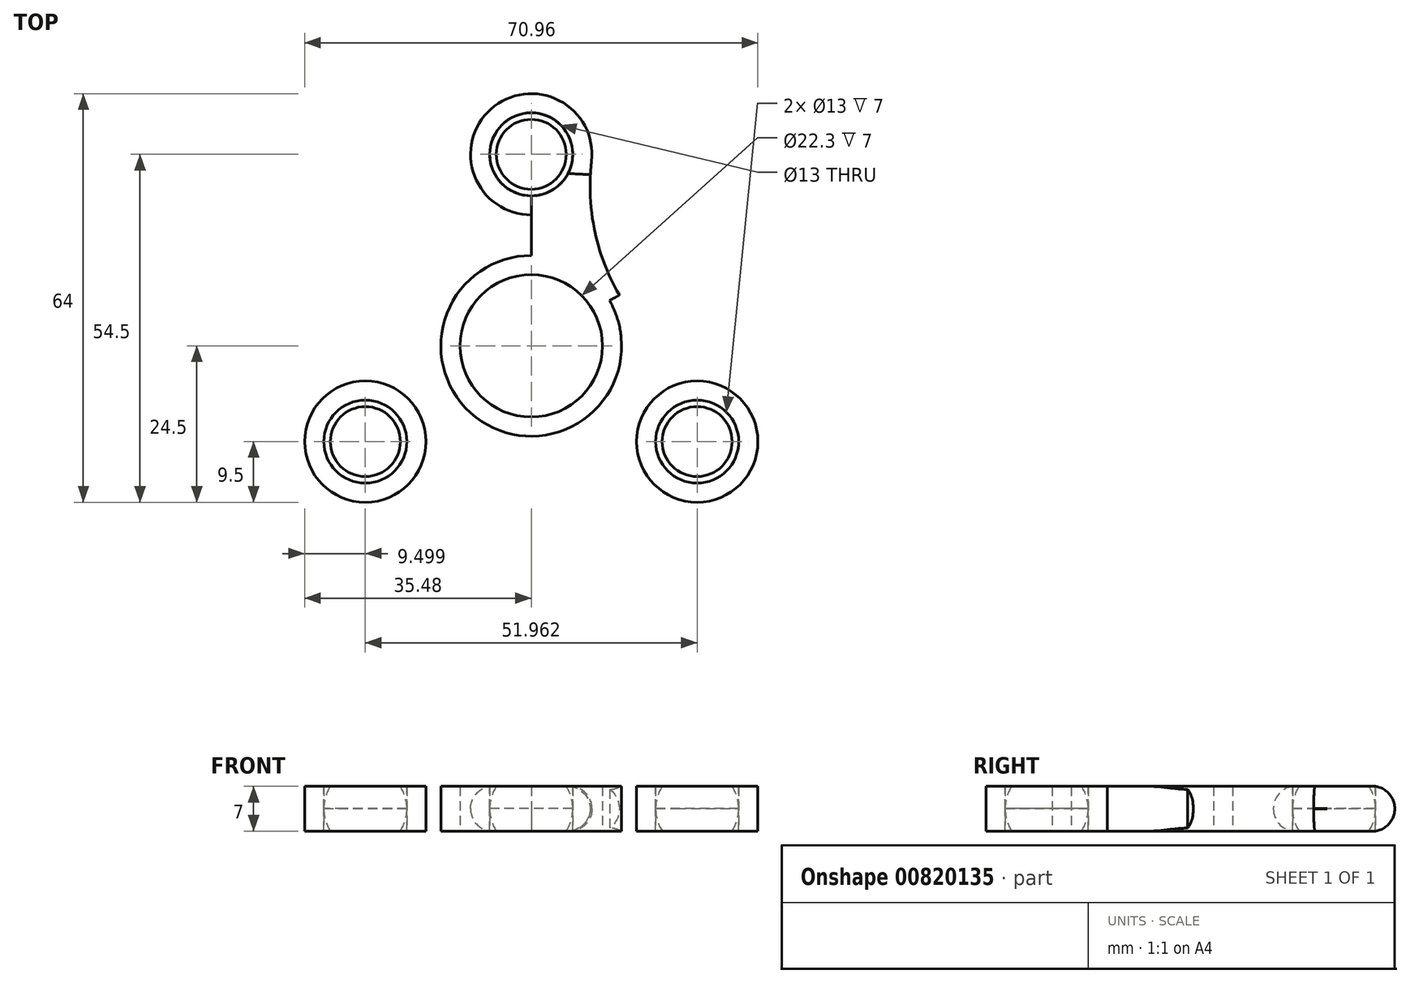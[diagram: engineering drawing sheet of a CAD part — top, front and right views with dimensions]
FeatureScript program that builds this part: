
annotation { "Feature Type Name" : "Feature", "Feature Type Description" : "" }
export const myFeature = defineFeature(function(context is Context, id is Id, definition is map)
    precondition{}
    {
        {
            var Q0;
            Q0=qCreatedBy(makeId("Top.planeOp"),FACE);
            var sketch = newSketch(context, id + "F0", { "sketchPlane" : qUnion([Q0])});
            skCircle(sketch, "E0", {"center": v(0, 0) * mm, "radius": 11.15 * mm});
            skCircle(sketch, "E1", {"center": v(0, 0) * mm, "radius": 14.15 * mm});
            skCircle(sketch, "E2", {"center": v(0, 30) * mm, "radius": 6.5 * mm});
            skCircle(sketch, "E3", {"center": v(0, 30) * mm, "radius": 9.5 * mm});
            skLineSegment(sketch, "E4", {"start": v(0, 30) * mm, "end": v(0, 0) * mm});
            skCircle(sketch, "E5.1.0", {"center": v(-25.98, -15) * mm, "radius": 9.5 * mm});
            skCircle(sketch, "E5.1.1", {"center": v(-25.98, -15) * mm, "radius": 6.5 * mm});
            skCircle(sketch, "E5.2.0", {"center": v(25.98, -15) * mm, "radius": 9.5 * mm});
            skCircle(sketch, "E5.2.1", {"center": v(25.98, -15) * mm, "radius": 6.5 * mm});
            skLineSegment(sketch, "E6", {"start": v(0, 0) * mm, "end": v(43.3, 25) * mm});
            skLineSegment(sketch, "E7", {"start": v(43.3, 25) * mm, "end": v(25.98, -15) * mm});
            skArc(sketch, "E8", {"start": v(29.76, -6.28) * mm, "mid": v(13.78, 7.96) * mm, "end": v(9.44, 28.91) * mm});
            skArc(sketch, "E9.1.0", {"start": v(-9.44, 28.91) * mm, "mid": v(-13.78, 7.96) * mm, "end": v(-29.76, -6.28) * mm});
            skArc(sketch, "E9.2.0", {"start": v(-20.32, -22.63) * mm, "mid": v(0, -15.91) * mm, "end": v(20.32, -22.63) * mm});
            skSolve(sketch);
        }
        {
            var Q0;
            {var subQ0=sQuery(id+"F0.wireOp",EDGE,"E4");var subQ1=sQuery(id+"F0.wireOp",EDGE,"E0");var subQ2=makeQuery(id+"F0.imprint","INTERSECT",VERTEX,{"derivedFrom":[subQ1,subQ0]});Q0=makeQuery(id+"F0.imprint","IMPRINT",FACE,{"disambiguationData":[TD([[makeQuery(id+"F0.imprint","IMPRINT",EDGE,{"disambiguationData":[TD([[subQ2,-1.0]])],"derivedFrom":subQ1}),-1.0]])]});}
            var Q1;
            {var subQ0=sQuery(id+"F0.wireOp",EDGE,"E9.1.0");Q1=makeQuery(id+"F0.imprint","IMPRINT",FACE,{"disambiguationData":[TD([[makeQuery(id+"F0.imprint","IMPRINT",EDGE,{"derivedFrom":subQ0}),1.0]])]});}
            var Q2;
            Q2=makeQuery(id+"F0.imprint","IMPRINT",FACE,{"disambiguationData":[TD([[makeQuery(id+"F0.imprint","IMPRINT",EDGE,{"derivedFrom":sQuery(id+"F0.wireOp",EDGE,"E5.1.1")}),-1.0]])]});
            var Q3;
            Q3=makeQuery(id+"F0.imprint","IMPRINT",FACE,{"disambiguationData":[TD([[makeQuery(id+"F0.imprint","IMPRINT",EDGE,{"derivedFrom":sQuery(id+"F0.wireOp",EDGE,"E5.2.1")}),-1.0]])]});
            var Q4;
            {var subQ0=sQuery(id+"F0.wireOp",EDGE,"E4");var subQ1=sQuery(id+"F0.wireOp",EDGE,"E0");var subQ2=makeQuery(id+"F0.imprint","INTERSECT",VERTEX,{"derivedFrom":[subQ1,subQ0]});Q4=makeQuery(id+"F0.imprint","IMPRINT",FACE,{"disambiguationData":[TD([[makeQuery(id+"F0.imprint","IMPRINT",EDGE,{"disambiguationData":[TD([[subQ2,1.0]])],"derivedFrom":subQ1}),-1.0]])]});}
            var Q5;
            {var subQ3=sQuery(id+"F0.wireOp",EDGE,"E1");var subQ5=sQuery(id+"F0.wireOp",EDGE,"E4");var subQ8=makeQuery(id+"F0.imprint","INTERSECT",VERTEX,{"derivedFrom":[subQ3,subQ5]});Q5=makeQuery(id+"F0.imprint","IMPRINT",FACE,{"disambiguationData":[TD([[makeQuery(id+"F0.imprint","IMPRINT",EDGE,{"disambiguationData":[TD([[subQ8,1.0]])],"derivedFrom":subQ3}),-1.0]])]});}
            var Q6;
            Q6=makeQuery(id+"F0.imprint","IMPRINT",FACE,{"disambiguationData":[TD([[makeQuery(id+"F0.imprint","IMPRINT",EDGE,{"derivedFrom":sQuery(id+"F0.wireOp",EDGE,"E2")}),-1.0]])]});
            extrude(context, id + "F1", {"entities" : qUnion([Q0, Q1, Q2, Q3, Q4, Q5, Q6]), "depth" : 7 * mm, "offsetDistance" : 25 * mm});
        }
        {
            var Q0;
            Q0=qCreatedBy(makeId("Right.planeOp"),FACE);
            var sketch = newSketch(context, id + "F2", { "sketchPlane" : qUnion([Q0])});
            skLineSegment(sketch, "E10", {"start": v(23.5, 0) * mm, "end": v(23.5, 7) * mm});
            skLineSegment(sketch, "E11", {"start": v(36.5, 7) * mm, "end": v(36.5, 0) * mm});
            skLineSegment(sketch, "E12.0", {"start": v(23.5, 7) * mm, "end": v(36.5, 7) * mm});
            skLineSegment(sketch, "E13.0", {"start": v(23.5, 0) * mm, "end": v(36.5, 0) * mm});
            skLineSegment(sketch, "E14", {"start": v(30, 7) * mm, "end": v(30, 0) * mm});
            skCircle(sketch, "E15", {"center": v(30, 3.5) * mm, "radius": 6.5 * mm});
            skLineSegment(sketch, "E16", {"start": v(0, 0) * mm, "end": v(0, -53.5) * mm});
            skSolve(sketch);
        }
        {
            var Q0;
            {var subQ0=sQuery(id+"F2.wireOp",EDGE,"E13.0");var subQ1=sQuery(id+"F2.wireOp",EDGE,"E10");var subQ2=makeQuery(id+"F2.imprint","INTERSECT",VERTEX,{"derivedFrom":[subQ1,subQ0]});Q0=makeQuery(id+"F2.imprint","IMPRINT",FACE,{"disambiguationData":[TD([[makeQuery(id+"F2.imprint","IMPRINT",EDGE,{"disambiguationData":[TD([[subQ2,-1.0]])],"derivedFrom":subQ1}),-1.0]])]});}
            var Q1;
            {var subQ0=sQuery(id+"F2.wireOp",EDGE,"E12.0");var subQ1=sQuery(id+"F2.wireOp",EDGE,"E10");var subQ2=makeQuery(id+"F2.imprint","INTERSECT",VERTEX,{"derivedFrom":[subQ1,subQ0]});Q1=makeQuery(id+"F2.imprint","IMPRINT",FACE,{"disambiguationData":[TD([[makeQuery(id+"F2.imprint","IMPRINT",EDGE,{"disambiguationData":[TD([[subQ2,1.0]])],"derivedFrom":subQ1}),-1.0]])]});}
            var Q2;
            Q2=sQuery(id+"F2.wireOp",EDGE,"E14");
            revolve(context, id + "F3", {"surfaceOperationType" : NewSurfaceOperationType.NEW, "entities" : qUnion([Q0, Q1]), "axis" : qUnion([Q2]), "revolveType" : RevolveType.FULL});
        }
        {
            var Q0;
            Q0=makeQuery(id+"F3.opRevolve","SWEPT_BODY",BODY,{"disambiguationData":[OSD([sQuery(id+"F2.wireOp",EDGE,"E10"),sQuery(id+"F2.wireOp",EDGE,"E13.0"),sQuery(id+"F2.wireOp",EDGE,"E15")])]});
            var Q1;
            Q1=makeQuery(id+"F3.opRevolve","SWEPT_BODY",BODY,{"disambiguationData":[OSD([sQuery(id+"F2.wireOp",EDGE,"E10"),sQuery(id+"F2.wireOp",EDGE,"E12.0"),sQuery(id+"F2.wireOp",EDGE,"E15")])]});
            var Q2;
            Q2=sQuery(id+"F2.wireOp",EDGE,"E16");
            circularPattern(context, id + "F4", {"entities" : qUnion([Q0, Q1]), "axis" : qUnion([Q2]), "angle" : 360 * degree, "instanceCount" : 3, "equalSpace" : true});
        }
        {
            var Q0;
            Q0=makeQuery(id+"F1.opExtrude","CAP_EDGE",EDGE,{"disambiguationData":[OSD([sQuery(id+"F0.wireOp",EDGE,"E8")])],"isStart":true});
            var Q1;
            Q1=makeQuery(id+"F1.opExtrude","CAP_EDGE",EDGE,{"disambiguationData":[OSD([sQuery(id+"F0.wireOp",EDGE,"E3")])],"isStart":true});
            var Q2;
            Q2=makeQuery(id+"F1.opExtrude","CAP_EDGE",EDGE,{"disambiguationData":[OSD([sQuery(id+"F0.wireOp",EDGE,"E8")])],"isStart":false});
            fillet(context, id + "F5", {"entities" : qUnion([Q0, Q1, Q2]), "radius" : 3.5 * mm, "tangentPropagation" : true, "allowEdgeOverflow" : false});
        }
    });
